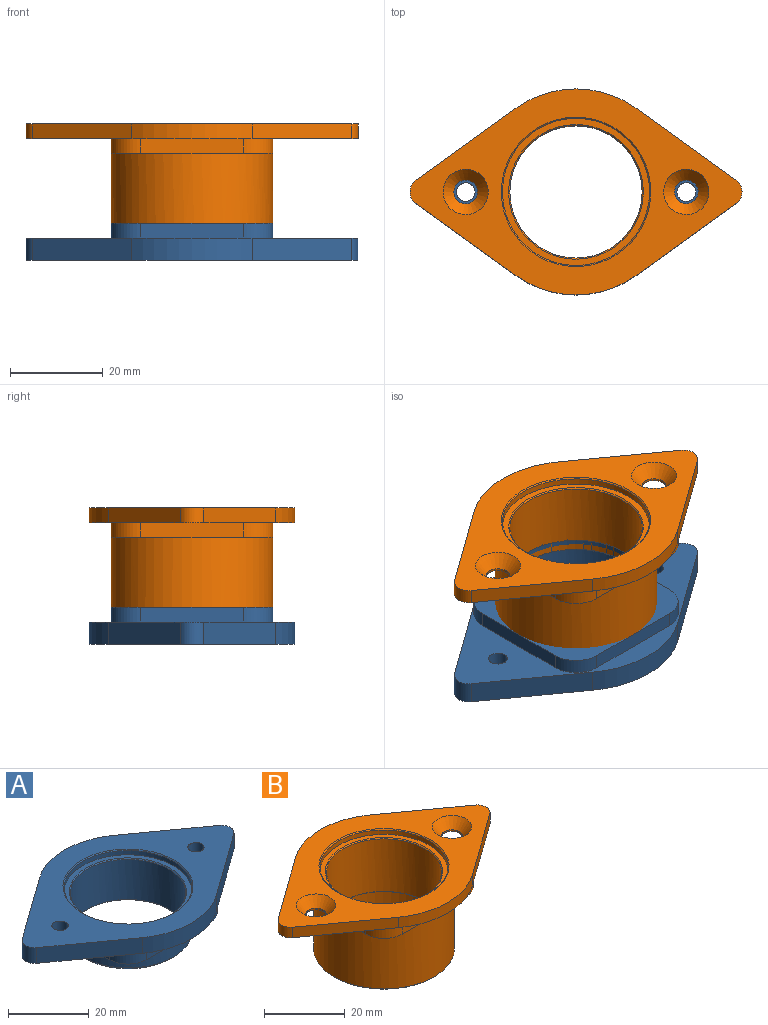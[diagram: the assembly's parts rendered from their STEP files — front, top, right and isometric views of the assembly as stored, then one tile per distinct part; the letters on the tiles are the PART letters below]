
ASSEMBLY  parts=2 mates=3
PART A: 30 faces, bbox 71.7x44.5x14.3 mm
  f0: cylinder r=3.17mm len=5.16mm, axis (0,0,-1), area 28.7mm2, adj f11,f13,f14,f18
  f1: cone r=15.07mm half-angle=45deg, axis (0,0,1), area 109.1mm2, adj f5,f24
  f2: cone r=14.52mm half-angle=45deg, axis (0,0,-1), area 32mm2, adj f9,f24
  f3: cone r=14.27mm half-angle=45deg, axis (0,0,1), area 32mm2, adj f9,f23
  f4: cone r=15.86mm half-angle=45deg, axis (0,0,1), area 35.5mm2, adj f8,f18
  f5: cylinder r=15.86mm len=31.72mm, axis (0,0,1), area 553.8mm2, adj f1,f10
  f6: cylinder r=2.02mm len=4.76mm, axis (0,0,1), area 60.4mm2, adj f11,f18
  f7: cylinder r=2.02mm len=4.76mm, axis (0,0,1), area 60.4mm2, adj f11,f18
  f8: cylinder r=15.86mm len=31.72mm, axis (0,0,1), area 133.3mm2, adj f4,f23
  f9: cylinder r=14.27mm len=28.55mm, axis (0,0,-1), area 1094.2mm2, adj f2,f3
  f10: plane 34.93x34.93mm, normal (0,0,-1), area 394.7mm2, adj f5,f19,f20,f21,f22,f25,f26,f27
  f11: plane 71.66x44.45mm, normal (0,0,-1), area 771.1mm2, adj f0,f6,f7,f12,f13,f14,f15,f16
  f12: cylinder r=22.23mm len=25.93mm, axis (0,0,-1), area 131.8mm2, adj f11,f13,f17,f18
  f13: plane 21.54x15.47mm, normal (-0.58,0.81,0), area 126.3mm2, adj f0,f11,f12,f18
  f14: plane 21.54x15.47mm, normal (-0.58,-0.81,0), area 126.3mm2, adj f0,f11,f15,f18
  f15: cylinder r=22.23mm len=25.93mm, axis (0,0,-1), area 131.8mm2, adj f11,f14,f16,f18
  f16: plane 21.54x15.47mm, normal (0.58,-0.81,0), area 126.3mm2, adj f11,f15,f18,f29
  f17: plane 21.54x15.47mm, normal (0.58,0.81,0), area 126.3mm2, adj f11,f12,f18,f29
  f18: plane 71.66x44.45mm, normal (0,0,1), area 1140.7mm2, adj f0,f4,f6,f7,f12,f13,f14,f15
  f19: plane 22.23x3.18mm, normal (-1,0,0), area 70.6mm2, adj f10,f11,f26,f27
  f20: plane 22.23x3.18mm, normal (0,1,0), area 70.6mm2, adj f10,f11,f27,f28
  f21: plane 22.23x3.18mm, normal (1,0,0), area 70.6mm2, adj f10,f11,f25,f28
  f22: plane 22.23x3.18mm, normal (0,-1,0), area 70.6mm2, adj f10,f11,f25,f26
  f23: plane 31.72x31.72mm, normal (0,0,1), area 127.7mm2, adj f3,f8
  f24: plane 30.14x30.14mm, normal (0,0,-1), area 50.6mm2, adj f1,f2
  f25: cylinder r=6.35mm len=6.35mm, axis (0,0,1), area 31.7mm2, adj f10,f11,f21,f22
  f26: cylinder r=6.35mm len=6.35mm, axis (0,0,1), area 31.7mm2, adj f10,f11,f19,f22
  f27: cylinder r=6.35mm len=6.35mm, axis (0,0,1), area 31.7mm2, adj f10,f11,f19,f20
  f28: cylinder r=6.35mm len=6.35mm, axis (0,0,1), area 31.7mm2, adj f10,f11,f20,f21
  f29: cylinder r=3.17mm len=5.16mm, axis (0,0,-1), area 28.7mm2, adj f11,f16,f17,f18
PART B: 38 faces, bbox 71.7x44.5x25.1 mm
  f0: cone r=15.87mm half-angle=45deg, axis (0,0,-1), area 35.5mm2, adj f11,f30
  f1: cone r=17.21mm half-angle=45deg, axis (0,0,1), area 38.5mm2, adj f12,f30
  f2: cone r=14.27mm half-angle=45deg, axis (0,0,-1), area 32mm2, adj f13,f31
  f3: cone r=14.27mm half-angle=45deg, axis (0,0,1), area 32mm2, adj f13,f37
  f4: cone r=15.88mm half-angle=45deg, axis (0,0,1), area 35.5mm2, adj f9,f25
  f5: cone r=4.89mm half-angle=41deg, axis (0,0,1), area 83.3mm2, adj f6,f25
  f6: cylinder r=2.55mm len=5.11mm, axis (0,0,1), area 7.8mm2, adj f5,f18
  f7: cone r=4.89mm half-angle=41deg, axis (0,0,1), area 83.3mm2, adj f8,f25
  f8: cylinder r=2.55mm len=5.11mm, axis (0,0,1), area 7.8mm2, adj f7,f18
  f9: cylinder r=15.88mm len=31.75mm, axis (0,0,1), area 133.4mm2, adj f4,f37
  f10: cylinder r=3.17mm len=5.16mm, axis (0,0,-1), area 19.1mm2, adj f18,f20,f21,f25
  f11: cylinder r=15.87mm len=31.74mm, axis (0,0,-1), area 687.3mm2, adj f0,f31
  f12: cylinder r=17.46mm len=34.93mm, axis (0,0,1), area 2034.9mm2, adj f1,f14,f15,f16,f17
  f13: cylinder r=14.27mm len=28.55mm, axis (0,0,-1), area 1427.4mm2, adj f2,f3
  f14: plane 17.46x17.46mm, normal (0,0,-1), area 56.8mm2, adj f12,f26,f27,f34
  f15: plane 17.46x17.46mm, normal (0,0,-1), area 56.8mm2, adj f12,f27,f28,f35
  f16: plane 17.46x17.46mm, normal (0,0,-1), area 56.8mm2, adj f12,f28,f29,f32
  f17: plane 17.46x17.46mm, normal (0,0,-1), area 56.8mm2, adj f12,f26,f29,f33
  f18: plane 71.66x44.45mm, normal (0,0,-1), area 755.8mm2, adj f6,f8,f10,f19,f20,f21,f22,f23
  f19: cylinder r=22.23mm len=25.93mm, axis (0,0,-1), area 87.9mm2, adj f18,f20,f24,f25
  f20: plane 21.54x15.47mm, normal (-0.58,0.81,0), area 84.2mm2, adj f10,f18,f19,f25
  f21: plane 21.54x15.47mm, normal (-0.58,-0.81,0), area 84.2mm2, adj f10,f18,f22,f25
  f22: cylinder r=22.23mm len=25.93mm, axis (0,0,-1), area 87.9mm2, adj f18,f21,f23,f25
  f23: plane 21.54x15.47mm, normal (0.58,-0.81,0), area 84.2mm2, adj f18,f22,f25,f36
  f24: plane 21.54x15.47mm, normal (0.58,0.81,0), area 84.2mm2, adj f18,f19,f25,f36
  f25: plane 71.66x44.45mm, normal (0,0,1), area 1014.8mm2, adj f4,f5,f7,f10,f19,f20,f21,f22
  f26: plane 22.23x3.18mm, normal (-1,0,0), area 70.6mm2, adj f14,f17,f18,f33,f34
  f27: plane 22.23x3.18mm, normal (0,1,0), area 70.6mm2, adj f14,f15,f18,f34,f35
  f28: plane 22.23x3.18mm, normal (1,0,0), area 70.6mm2, adj f15,f16,f18,f32,f35
  f29: plane 22.23x3.18mm, normal (0,-1,0), area 70.6mm2, adj f16,f17,f18,f32,f33
  f30: plane 34.43x34.43mm, normal (0,0,-1), area 114.5mm2, adj f0,f1
  f31: plane 31.74x31.74mm, normal (0,0,-1), area 128.3mm2, adj f2,f11
  f32: cylinder r=6.35mm len=6.35mm, axis (0,0,1), area 31.7mm2, adj f16,f18,f28,f29
  f33: cylinder r=6.35mm len=6.35mm, axis (0,0,1), area 31.7mm2, adj f17,f18,f26,f29
  f34: cylinder r=6.35mm len=6.35mm, axis (0,0,1), area 31.7mm2, adj f14,f18,f26,f27
  f35: cylinder r=6.35mm len=6.35mm, axis (0,0,1), area 31.7mm2, adj f15,f18,f27,f28
  f36: cylinder r=3.17mm len=5.16mm, axis (0,0,-1), area 19.1mm2, adj f18,f23,f24,f25
  f37: plane 31.75x31.75mm, normal (0,0,1), area 128.9mm2, adj f3,f9
PLACE A rot(axis=(1,0,0),180deg) t=(20.46,-1.91,-24.83)mm
PLACE B t=(20.46,-1.91,0.59)mm fixed
MATE cylindrical A.f7 <-> B.f7  axis (0,0,-1) through (44.27,-1.91,-27.21)mm
MATE parallel A.f25 <-> B.f0  axis (0,0,1) through (31.57,9.2,-19.27)mm
MATE revolute A.f1 <-> B.f0  axis (0,0,1) through (20.46,-1.91,-19.27)mm
